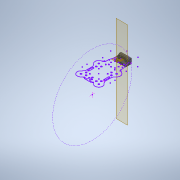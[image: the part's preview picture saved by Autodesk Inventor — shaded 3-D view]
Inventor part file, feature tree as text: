
AUTODESK INVENTOR PART (.ipt)
format: ipt  version: 2020 (Build 240168000, 168)  size: 660,480 bytes
history: native  units: in
note: dims shown in document units (in); Inventor stores cm internally (conversion verified against a paired STEP export)
features: sketch x20, extrude x17, projected_geometry x9, plane x7
ambient origin geometry x8: Origin, YZ Plane, XZ Plane, XY Plane, X Axis, Y Axis, Z Axis, Center Point
bodies: Solid2 (feature_tree)
feature tree (53):
  plane  "Work Plane1"
  plane  "Work Plane7"
  plane  "Work Plane4"
  plane  "Work Plane9"
  sketch  "Sketch13"  dims[d22=0.1181in d23=0.0in d24=0.2008in]
  plane  "Work Plane11"
  extrude  "Extrusion10"  Depth=0.2008in
  plane  "Work Plane8"
  sketch  "Sketch15"  dims[d35=0.0001in d36=1.378in d37=0.0in]
  extrude  "Extrusion12"  Depth=1.378in TaperAngle=0.0deg
  extrude  "Extrusion13"  Depth=1.378in TaperAngle=0.0deg
  extrude  "Extrusion14"  Depth=0.2244in
  extrude  "Extrusion15"  Depth=1.378in TaperAngle=0.0deg
  sketch  "Sketch20"  dims[d47=0.1181in d48=0.1181in d49=0.0in]
  extrude  "Extrusion16"  Depth=0.1181in
  extrude  "Extrusion17"  Depth=0.1181in TaperAngle=0.0deg
  extrude  "Extrusion18"  Depth=0.0394in TaperAngle=0.0deg
  extrude  "Extrusion19"  Depth=0.0394in TaperAngle=0.0deg
  extrude  "Extrusion20"  Depth=0.1575in TaperAngle=0.0deg
  extrude  "Extrusion21"  Depth=0.0787in TaperAngle=0.0deg
  extrude  "Extrusion22"  [1 undecoded]
  extrude  "Extrusion23"  Depth=0.0787in
  extrude  "Extrusion24"  Depth=0.1378in TaperAngle=0.0deg
  extrude  "Extrusion25"  Depth=1.9685in
  plane  "Work Plane12"
  extrude  "Extrusion26"  Depth=1.9685in
  extrude  "Extrusion27"  Depth=1.9685in
  sketch  "Sketch32"  dims[d14=1.9685in]
  sketch  "Sketch33"  dims[d34=0.0197in]
  sketch  "Sketch14"  dims[d25=0.2008in d32=1.378in d33=0.0in]
  sketch  "Sketch17"  dims[d38=0.0in d39=0.0in d40=0.2244in]
  sketch  "Sketch18"  dims[d41=0.2244in d42=1.378in d43=0.0in]
  projected_geometry  "Projected Loop7"
  projected_geometry  "Projected Loop8"
  sketch  "Sketch19"  dims[d44=0.1181in d45=0.0in d46=0.1181in]
  sketch  "Sketch21"  dims[d50=0.0394in d51=0.0in d52=0.0394in d53=0.0in]
  sketch  "Sketch22"  dims[d60=0.0118in d61=0.0394in d62=0.0in]
  projected_geometry  "Projected Loop9"
  sketch  "Sketch23"  dims[d63=0.1575in d64=0.0in d65=0.2963in d66=0.0in]
  projected_geometry  "Projected Loop10"
  projected_geometry  "Projected Loop11"
  sketch  "Sketch24"  dims[d67=0.0787in d68=0.0in d69=0.0787in d70=0.0in]
  sketch  "Sketch25"  dims[d71=0.3937in d72=0.0in d73=-3.0625in]
  projected_geometry  "Projected Loop12"
  sketch  "Sketch26"  dims[d74=0.0787in d75=0.0787in]
  projected_geometry  "Projected Loop13"
  sketch  "Sketch27"  dims[d76=0.2938in d77=0.0in d78=0.1378in d79=0.0in]
  projected_geometry  "Projected Loop14"
  sketch  "Sketch28"  dims[d2=0.0197in d3=1.9685in]
  projected_geometry  "Projected Loop15"
  sketch  "Sketch29"  dims[d4=0.0197in d5=1.9685in]
  sketch  "Sketch30"  dims[d11=0.0197in d12=1.9685in]
  sketch  "Sketch31"  dims[d13=0.0197in]
note: 1 required parameter value undecoded (feature->parameter linkage not recoverable at this tier; creation-order binding heuristic only, values carry confidence <= 0.55)
